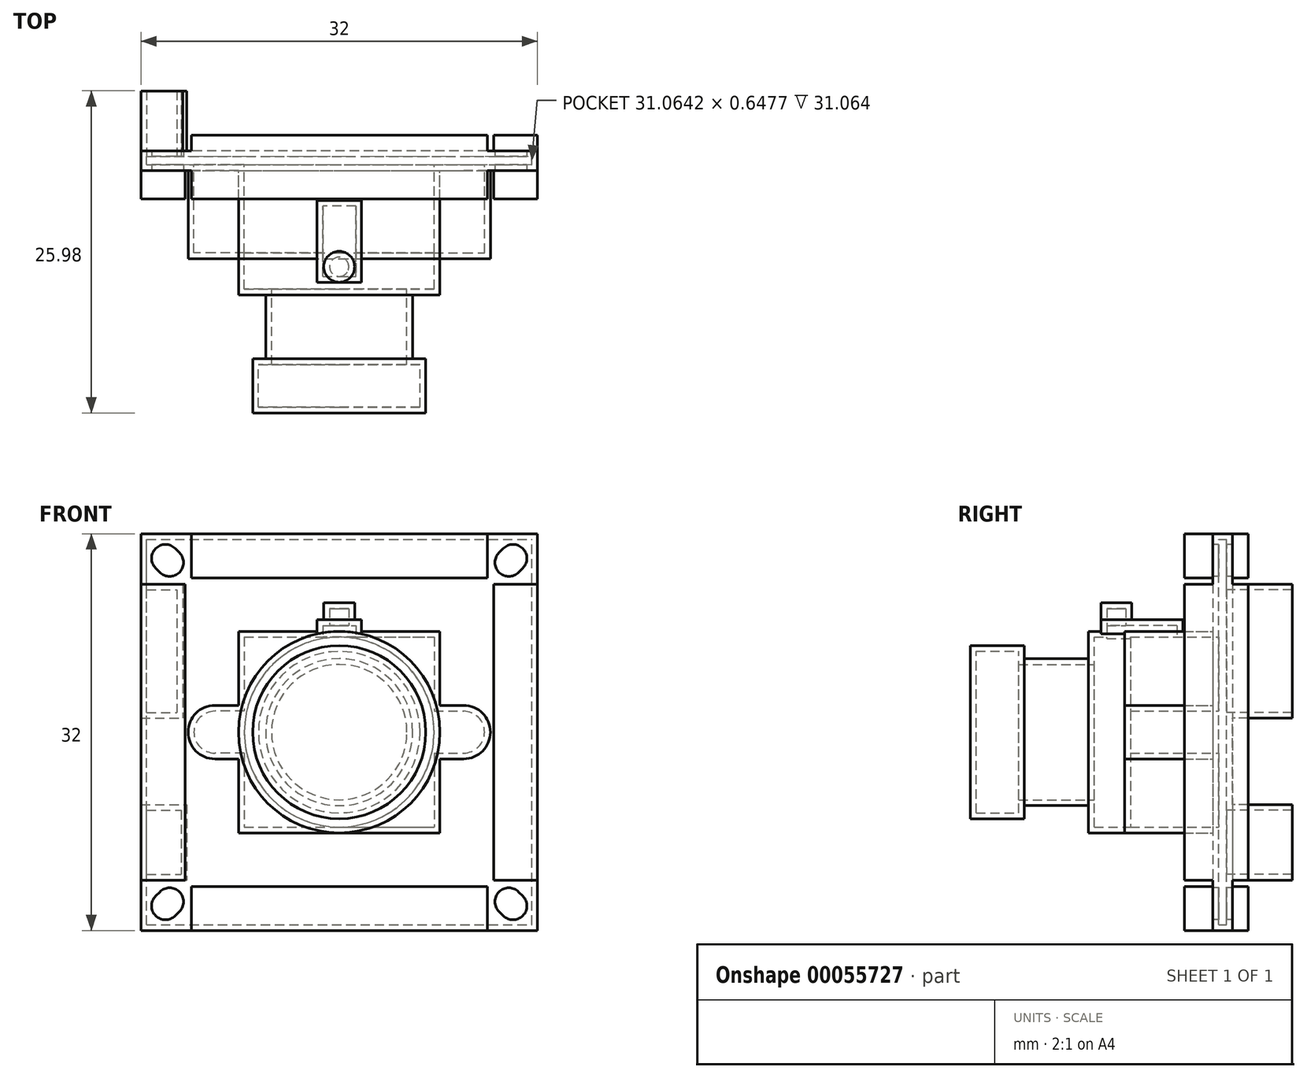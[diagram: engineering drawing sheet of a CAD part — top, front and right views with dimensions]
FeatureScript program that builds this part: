
annotation { "Feature Type Name" : "Feature", "Feature Type Description" : "" }
export const myFeature = defineFeature(function(context is Context, id is Id, definition is map)
    precondition{}
    {
        {
            var Q0;
            Q0=qCreatedBy(makeId("Front.planeOp"),FACE);
            var sketch = newSketch(context, id + "F0", { "sketchPlane" : qUnion([Q0])});
            skLineSegment(sketch, "E0.bottom", {"start": v(-16, -16) * mm, "end": v(16, -16) * mm});
            skLineSegment(sketch, "E0.top", {"start": v(-16, 16) * mm, "end": v(16, 16) * mm});
            skLineSegment(sketch, "E0.left", {"start": v(-16, -16) * mm, "end": v(-16, 16) * mm});
            skLineSegment(sketch, "E0.right", {"start": v(16, -16) * mm, "end": v(16, 16) * mm});
            skLineSegment(sketch, "E1", {"start": v(-16, -16) * mm, "end": v(16, 16) * mm});
            skSolve(sketch);
        }
        {
            var Q0;
            Q0=qSketchRegion(id+"F0",true);
            extrude(context, id + "F1", {"entities" : qUnion([Q0]), "depth" : 1.59 * mm});
        }
        {
            var Q0;
            Q0=makeQuery(id+"F1.opExtrude","CAP_FACE",FACE,{"disambiguationData":[OSD([sQuery(id+"F0.wireOp",EDGE,"E0.bottom"),sQuery(id+"F0.wireOp",EDGE,"E0.top"),sQuery(id+"F0.wireOp",EDGE,"E0.left"),sQuery(id+"F0.wireOp",EDGE,"E0.right")])],"isStart":false});
            var sketch = newSketch(context, id + "F2", { "sketchPlane" : qUnion([Q0])});
            skLineSegment(sketch, "E2.bottom", {"start": v(-8.13, 8.13) * mm, "end": v(8.13, 8.13) * mm});
            skLineSegment(sketch, "E2.top", {"start": v(-8.13, -8.13) * mm, "end": v(8.13, -8.13) * mm});
            skLineSegment(sketch, "E2.left", {"start": v(-8.13, 8.13) * mm, "end": v(-8.13, 2.16) * mm});
            skLineSegment(sketch, "E2.right", {"start": v(8.13, 8.13) * mm, "end": v(8.13, 2.16) * mm});
            skLineSegment(sketch, "E3", {"start": v(-8.13, -8.13) * mm, "end": v(8.13, 8.13) * mm});
            skLineSegment(sketch, "E4", {"start": v(8.13, 2.16) * mm, "end": v(10.03, 2.16) * mm});
            skLineSegment(sketch, "E5", {"start": v(8.13, -2.16) * mm, "end": v(10.03, -2.16) * mm});
            skArc(sketch, "E6", {"start": v(10.03, -2.16) * mm, "mid": v(12.2, 0) * mm, "end": v(10.03, 2.16) * mm});
            skLineSegment(sketch, "E7", {"start": v(0, 0) * mm, "end": v(10.03, 0) * mm, "construction": true});
            skLineSegment(sketch, "E8.trimOffspring", {"start": v(8.13, -2.16) * mm, "end": v(8.13, -8.13) * mm});
            skLineSegment(sketch, "E9", {"start": v(0, 0) * mm, "end": v(0, 8.13) * mm});
            skLineSegment(sketch, "E10.0.MirrorCS", {"start": v(-8.13, 2.16) * mm, "end": v(-10.03, 2.16) * mm});
            skArc(sketch, "E11.0.MirrorCS", {"start": v(-10.03, -2.16) * mm, "mid": v(-12.2, 0) * mm, "end": v(-10.03, 2.16) * mm});
            skLineSegment(sketch, "E12.0.MirrorCS", {"start": v(-8.13, -2.16) * mm, "end": v(-10.03, -2.16) * mm});
            skLineSegment(sketch, "E13.trimOffspring", {"start": v(-8.13, -2.16) * mm, "end": v(-8.13, -8.13) * mm});
            skSolve(sketch);
        }
        {
            var Q0;
            Q0=qSketchRegion(id+"F2",true);
            extrude(context, id + "F3", {"entities" : qUnion([Q0]), "operationType" : NewBodyOperationType.ADD, "depth" : 7.11 * mm});
        }
        {
            var Q0;
            Q0=makeQuery(id+"F3.opExtrude","CAP_FACE",FACE,{"disambiguationData":[OSD([sQuery(id+"F2.wireOp",EDGE,"E2.bottom"),sQuery(id+"F2.wireOp",EDGE,"E2.top"),sQuery(id+"F2.wireOp",EDGE,"E2.left"),sQuery(id+"F2.wireOp",EDGE,"E2.right"),sQuery(id+"F2.wireOp",EDGE,"E4"),sQuery(id+"F2.wireOp",EDGE,"E5"),sQuery(id+"F2.wireOp",EDGE,"E6"),sQuery(id+"F2.wireOp",EDGE,"E8.trimOffspring"),sQuery(id+"F2.wireOp",EDGE,"E10.0.MirrorCS"),sQuery(id+"F2.wireOp",EDGE,"E11.0.MirrorCS"),sQuery(id+"F2.wireOp",EDGE,"E12.0.MirrorCS"),sQuery(id+"F2.wireOp",EDGE,"E13.trimOffspring")])],"isStart":false});
            var sketch = newSketch(context, id + "F4", { "sketchPlane" : qUnion([Q0])});
            skCircle(sketch, "E14", {"center": v(0, 0) * mm, "radius": 8.13 * mm});
            skSolve(sketch);
        }
        {
            var Q0;
            Q0=qSketchRegion(id+"F4",true);
            extrude(context, id + "F5", {"entities" : qUnion([Q0]), "operationType" : NewBodyOperationType.ADD, "depth" : 2.92 * mm});
        }
        {
            var Q0;
            Q0=makeQuery(id+"F5.opExtrude","CAP_FACE",FACE,{"disambiguationData":[OSD([sQuery(id+"F4.wireOp",EDGE,"E14")])],"isStart":false});
            var sketch = newSketch(context, id + "F6", { "sketchPlane" : qUnion([Q0])});
            skCircle(sketch, "E15", {"center": v(0, 0) * mm, "radius": 5.93 * mm});
            skSolve(sketch);
        }
        {
            var Q0;
            Q0=qSketchRegion(id+"F6",true);
            extrude(context, id + "F7", {"entities" : qUnion([Q0]), "operationType" : NewBodyOperationType.ADD, "depth" : 5.16 * mm});
        }
        {
            var Q0;
            Q0=makeQuery(id+"F7.opExtrude","CAP_FACE",FACE,{"disambiguationData":[OSD([sQuery(id+"F6.wireOp",EDGE,"E15")])],"isStart":false});
            var sketch = newSketch(context, id + "F8", { "sketchPlane" : qUnion([Q0])});
            skCircle(sketch, "E16", {"center": v(0, 0) * mm, "radius": 6.99 * mm});
            skSolve(sketch);
        }
        {
            var Q0;
            Q0=qSketchRegion(id+"F8",true);
            extrude(context, id + "F9", {"entities" : qUnion([Q0]), "operationType" : NewBodyOperationType.ADD, "depth" : 4.37 * mm});
        }
        {
            var Q0;
            Q0=makeQuery(id+"F3.opExtrude","SWEPT_FACE",FACE,{"disambiguationData":[OSD([sQuery(id+"F2.wireOp",EDGE,"E2.bottom")])]});
            var sketch = newSketch(context, id + "F10", { "sketchPlane" : qUnion([Q0])});
            skLineSegment(sketch, "E17.bottom", {"start": v(-1.8, -4) * mm, "end": v(1.8, -4) * mm});
            skLineSegment(sketch, "E17.top", {"start": v(-1.8, -10.6) * mm, "end": v(1.8, -10.6) * mm});
            skLineSegment(sketch, "E17.left", {"start": v(-1.8, -4) * mm, "end": v(-1.8, -10.6) * mm});
            skLineSegment(sketch, "E17.right", {"start": v(1.8, -4) * mm, "end": v(1.8, -10.6) * mm});
            skSolve(sketch);
        }
        {
            var Q0;
            Q0=qSketchRegion(id+"F10",true);
            extrude(context, id + "F11", {"entities" : qUnion([Q0]), "operationType" : NewBodyOperationType.ADD, "depth" : 0.94 * mm, "hasSecondDirection" : true, "secondDirectionOppositeDirection" : true, "secondDirectionDepth" : 1.27 * mm});
        }
        {
            var Q0;
            Q0=makeQuery(id+"F11.opExtrude","CAP_FACE",FACE,{"disambiguationData":[OSD([sQuery(id+"F10.wireOp",EDGE,"E17.bottom"),sQuery(id+"F10.wireOp",EDGE,"E17.top"),sQuery(id+"F10.wireOp",EDGE,"E17.left"),sQuery(id+"F10.wireOp",EDGE,"E17.right")])],"isStart":false});
            var sketch = newSketch(context, id + "F12", { "sketchPlane" : qUnion([Q0])});
            skCircle(sketch, "E18", {"center": v(0, -9.36) * mm, "radius": 1.24 * mm});
            skSolve(sketch);
        }
        {
            var Q0;
            Q0=qSketchRegion(id+"F12",true);
            extrude(context, id + "F13", {"entities" : qUnion([Q0]), "operationType" : NewBodyOperationType.ADD, "depth" : 1.37 * mm});
        }
        {
            var Q0;
            Q0=makeQuery(id+"F1.opExtrude","CAP_FACE",FACE,{"disambiguationData":[OSD([sQuery(id+"F0.wireOp",EDGE,"E0.bottom"),sQuery(id+"F0.wireOp",EDGE,"E0.top"),sQuery(id+"F0.wireOp",EDGE,"E0.left"),sQuery(id+"F0.wireOp",EDGE,"E0.right")])],"isStart":true});
            var sketch = newSketch(context, id + "F14", { "sketchPlane" : qUnion([Q0])});
            skLineSegment(sketch, "E19.bottom", {"start": v(16, 11.94) * mm, "end": v(12.62, 11.94) * mm});
            skLineSegment(sketch, "E19.top", {"start": v(16, 1.12) * mm, "end": v(12.62, 1.12) * mm});
            skLineSegment(sketch, "E19.left", {"start": v(16, 11.94) * mm, "end": v(16, 1.12) * mm});
            skLineSegment(sketch, "E19.right", {"start": v(12.62, 11.94) * mm, "end": v(12.62, 1.12) * mm});
            skLineSegment(sketch, "E20.bottom", {"start": v(16, -5.84) * mm, "end": v(12.3, -5.84) * mm});
            skLineSegment(sketch, "E20.top", {"start": v(16, -11.94) * mm, "end": v(12.3, -11.94) * mm});
            skLineSegment(sketch, "E20.left", {"start": v(16, -5.84) * mm, "end": v(16, -11.94) * mm});
            skLineSegment(sketch, "E20.right", {"start": v(12.3, -5.84) * mm, "end": v(12.3, -11.94) * mm});
            skSolve(sketch);
        }
        {
            var Q0;
            Q0=qSketchRegion(id+"F14",true);
            extrude(context, id + "F15", {"entities" : qUnion([Q0]), "operationType" : NewBodyOperationType.ADD, "depth" : 4.83 * mm});
        }
        {
            var Q0;
            Q0=makeQuery(id+"F15.opExtrude","CAP_FACE",FACE,{"disambiguationData":[OSD([sQuery(id+"F14.wireOp",EDGE,"E19.bottom"),sQuery(id+"F14.wireOp",EDGE,"E19.top"),sQuery(id+"F14.wireOp",EDGE,"E19.left"),sQuery(id+"F14.wireOp",EDGE,"E19.right")])],"isStart":false});
            var Q1;
            Q1=makeQuery(id+"F15.opExtrude","CAP_FACE",FACE,{"disambiguationData":[OSD([sQuery(id+"F14.wireOp",EDGE,"E20.bottom"),sQuery(id+"F14.wireOp",EDGE,"E20.top"),sQuery(id+"F14.wireOp",EDGE,"E20.left"),sQuery(id+"F14.wireOp",EDGE,"E20.right")])],"isStart":false});
            shell(context, id + "F16", {"entities" : qUnion([Q0, Q1]), "thickness" : 0.47 * mm});
        }
        {
            var Q0;
            Q0=makeQuery(id+"F1.opExtrude","CAP_FACE",FACE,{"disambiguationData":[OSD([sQuery(id+"F0.wireOp",EDGE,"E0.bottom"),sQuery(id+"F0.wireOp",EDGE,"E0.top"),sQuery(id+"F0.wireOp",EDGE,"E0.left"),sQuery(id+"F0.wireOp",EDGE,"E0.right")])],"isStart":true});
            var sketch = newSketch(context, id + "F17", { "sketchPlane" : qUnion([Q0])});
            skLineSegment(sketch, "E21.bottom", {"start": v(11.94, 16) * mm, "end": v(-11.94, 16) * mm});
            skLineSegment(sketch, "E21.top", {"start": v(11.94, 12.45) * mm, "end": v(-11.94, 12.45) * mm});
            skLineSegment(sketch, "E21.left", {"start": v(11.94, 16) * mm, "end": v(11.94, 12.45) * mm});
            skLineSegment(sketch, "E21.right", {"start": v(-11.94, 16) * mm, "end": v(-11.94, 12.45) * mm});
            skLineSegment(sketch, "E22.bottom", {"start": v(-16, 11.94) * mm, "end": v(-12.45, 11.94) * mm});
            skLineSegment(sketch, "E22.top", {"start": v(-16, -11.94) * mm, "end": v(-12.45, -11.94) * mm});
            skLineSegment(sketch, "E22.left", {"start": v(-16, 11.94) * mm, "end": v(-16, -11.94) * mm});
            skLineSegment(sketch, "E22.right", {"start": v(-12.45, 11.94) * mm, "end": v(-12.45, -11.94) * mm});
            skLineSegment(sketch, "E23.bottom", {"start": v(-11.94, -16) * mm, "end": v(11.94, -16) * mm});
            skLineSegment(sketch, "E23.top", {"start": v(-11.94, -12.45) * mm, "end": v(11.94, -12.45) * mm});
            skLineSegment(sketch, "E23.left", {"start": v(-11.94, -16) * mm, "end": v(-11.94, -12.45) * mm});
            skLineSegment(sketch, "E23.right", {"start": v(11.94, -16) * mm, "end": v(11.94, -12.45) * mm});
            skSolve(sketch);
        }
        {
            var Q0;
            Q0=qSketchRegion(id+"F17",true);
            extrude(context, id + "F18", {"entities" : qUnion([Q0]), "operationType" : NewBodyOperationType.ADD, "depth" : 1.27 * mm});
        }
        {
            var Q0;
            Q0=makeQuery(id+"F1.opExtrude","CAP_FACE",FACE,{"disambiguationData":[OSD([sQuery(id+"F0.wireOp",EDGE,"E0.bottom"),sQuery(id+"F0.wireOp",EDGE,"E0.top"),sQuery(id+"F0.wireOp",EDGE,"E0.left"),sQuery(id+"F0.wireOp",EDGE,"E0.right")])],"isStart":false});
            var sketch = newSketch(context, id + "F19", { "sketchPlane" : qUnion([Q0])});
            skLineSegment(sketch, "E24.0.0", {"start": v(11.94, 12.45) * mm, "end": v(-11.94, 12.45) * mm});
            skLineSegment(sketch, "E24.0.1", {"start": v(-11.94, 12.45) * mm, "end": v(-11.94, 16) * mm});
            skLineSegment(sketch, "E24.0.2", {"start": v(-11.94, 16) * mm, "end": v(11.94, 16) * mm});
            skLineSegment(sketch, "E24.0.3", {"start": v(11.94, 16) * mm, "end": v(11.94, 12.45) * mm});
            skLineSegment(sketch, "E25.0.0", {"start": v(12.45, 11.94) * mm, "end": v(16, 11.94) * mm});
            skLineSegment(sketch, "E25.0.1", {"start": v(16, 11.94) * mm, "end": v(16, -11.94) * mm});
            skLineSegment(sketch, "E25.0.2", {"start": v(16, -11.94) * mm, "end": v(12.45, -11.94) * mm});
            skLineSegment(sketch, "E25.0.3", {"start": v(12.45, -11.94) * mm, "end": v(12.45, 11.94) * mm});
            skLineSegment(sketch, "E26.0.0", {"start": v(-11.94, -12.45) * mm, "end": v(11.94, -12.45) * mm});
            skLineSegment(sketch, "E26.0.1", {"start": v(11.94, -12.45) * mm, "end": v(11.94, -16) * mm});
            skLineSegment(sketch, "E26.0.2", {"start": v(11.94, -16) * mm, "end": v(-11.94, -16) * mm});
            skLineSegment(sketch, "E26.0.3", {"start": v(-11.94, -16) * mm, "end": v(-11.94, -12.45) * mm});
            skLineSegment(sketch, "E27.bottom", {"start": v(-16, 11.94) * mm, "end": v(-12.45, 11.94) * mm});
            skLineSegment(sketch, "E27.top", {"start": v(-16, -11.94) * mm, "end": v(-12.45, -11.94) * mm});
            skLineSegment(sketch, "E27.left", {"start": v(-16, 11.94) * mm, "end": v(-16, -11.94) * mm});
            skLineSegment(sketch, "E27.right", {"start": v(-12.45, 11.94) * mm, "end": v(-12.45, -11.94) * mm});
            skSolve(sketch);
        }
        {
            var Q0;
            Q0=qSketchRegion(id+"F19",true);
            extrude(context, id + "F20", {"entities" : qUnion([Q0]), "operationType" : NewBodyOperationType.ADD, "depth" : 2.3 * mm});
        }
        {
            var Q0;
            Q0=makeQuery(id+"F1.opExtrude","CAP_FACE",FACE,{"disambiguationData":[OSD([sQuery(id+"F0.wireOp",EDGE,"E0.bottom"),sQuery(id+"F0.wireOp",EDGE,"E0.top"),sQuery(id+"F0.wireOp",EDGE,"E0.left"),sQuery(id+"F0.wireOp",EDGE,"E0.right")])],"isStart":false});
            var sketch = newSketch(context, id + "F21", { "sketchPlane" : qUnion([Q0])});
            skLineSegment(sketch, "E28", {"start": v(14.47, 12.89) * mm, "end": v(14.81, 13.23) * mm});
            skLineSegment(sketch, "E29", {"start": v(12.89, 14.47) * mm, "end": v(13.23, 14.81) * mm});
            skArc(sketch, "E30", {"start": v(14.81, 13.23) * mm, "mid": v(14.81, 14.81) * mm, "end": v(13.23, 14.81) * mm});
            skArc(sketch, "E31", {"start": v(12.89, 14.47) * mm, "mid": v(12.89, 12.89) * mm, "end": v(14.47, 12.89) * mm});
            skLineSegment(sketch, "E32", {"start": v(13.68, 13.68) * mm, "end": v(16, 16) * mm, "construction": true});
            skLineSegment(sketch, "E33", {"start": v(0, 0) * mm, "end": v(0, 16) * mm, "construction": true});
            skLineSegment(sketch, "E34", {"start": v(0, 0) * mm, "end": v(10.03, 0) * mm, "construction": true});
            skArc(sketch, "E35.0.MirrorCS", {"start": v(-12.89, 14.47) * mm, "mid": v(-12.89, 12.89) * mm, "end": v(-14.47, 12.89) * mm});
            skLineSegment(sketch, "E36.0.MirrorCS", {"start": v(-12.89, 14.47) * mm, "end": v(-13.23, 14.81) * mm});
            skArc(sketch, "E37.0.MirrorCS", {"start": v(-14.81, 13.23) * mm, "mid": v(-14.81, 14.81) * mm, "end": v(-13.23, 14.81) * mm});
            skLineSegment(sketch, "E38.0.MirrorCS", {"start": v(-14.47, 12.89) * mm, "end": v(-14.81, 13.23) * mm});
            skArc(sketch, "E39.0.MirrorCS", {"start": v(-12.89, -14.47) * mm, "mid": v(-12.89, -12.89) * mm, "end": v(-14.47, -12.89) * mm});
            skLineSegment(sketch, "E40.0.MirrorCS", {"start": v(-14.47, -12.89) * mm, "end": v(-14.81, -13.23) * mm});
            skArc(sketch, "E41.0.MirrorCS", {"start": v(-14.81, -13.23) * mm, "mid": v(-14.81, -14.81) * mm, "end": v(-13.23, -14.81) * mm});
            skLineSegment(sketch, "E42.0.MirrorCS", {"start": v(-12.89, -14.47) * mm, "end": v(-13.23, -14.81) * mm});
            skArc(sketch, "E43.0.MirrorCS", {"start": v(14.81, -13.23) * mm, "mid": v(14.81, -14.81) * mm, "end": v(13.23, -14.81) * mm});
            skLineSegment(sketch, "E44.0.MirrorCS", {"start": v(14.47, -12.89) * mm, "end": v(14.81, -13.23) * mm});
            skArc(sketch, "E45.0.MirrorCS", {"start": v(12.89, -14.47) * mm, "mid": v(12.89, -12.89) * mm, "end": v(14.47, -12.89) * mm});
            skLineSegment(sketch, "E46.0.MirrorCS", {"start": v(12.89, -14.47) * mm, "end": v(13.23, -14.81) * mm});
            skSolve(sketch);
        }
        {
            var Q0;
            Q0=qSketchRegion(id+"F21",true);
            extrude(context, id + "F22", {"entities" : qUnion([Q0]), "operationType" : NewBodyOperationType.REMOVE, "endBound" : BoundingType.THROUGH_ALL, "oppositeDirection" : true, "depth" : 25.4 * mm});
        }
    });
